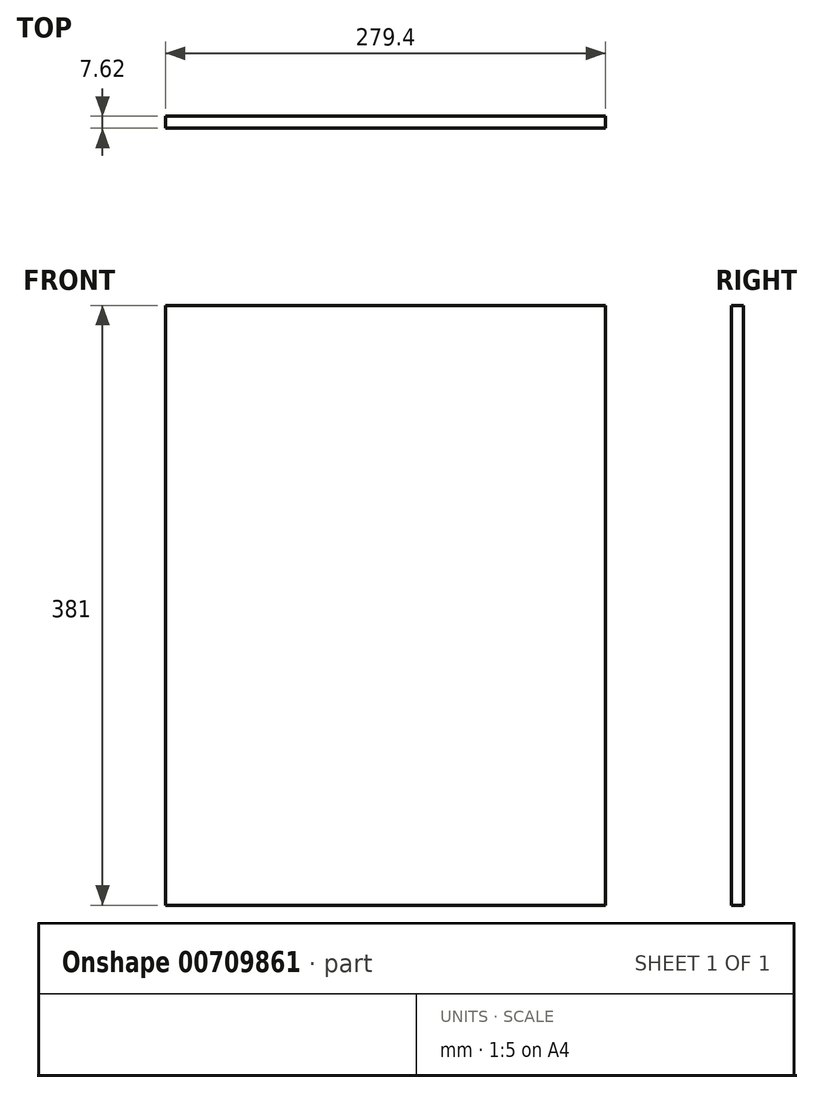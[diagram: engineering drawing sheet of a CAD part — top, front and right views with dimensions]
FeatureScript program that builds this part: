
annotation { "Feature Type Name" : "Feature", "Feature Type Description" : "" }
export const myFeature = defineFeature(function(context is Context, id is Id, definition is map)
    precondition{}
    {
        {
            var Q0;
            Q0=qCreatedBy(makeId("Front.planeOp"),FACE);
            var sketch = newSketch(context, id + "F0", { "sketchPlane" : qUnion([Q0])});
            skLineSegment(sketch, "E0.bottom", {"start": v(-157.96, 45.7) * mm, "end": v(121.44, 45.7) * mm});
            skLineSegment(sketch, "E0.top", {"start": v(-157.96, -335.3) * mm, "end": v(121.44, -335.3) * mm});
            skLineSegment(sketch, "E0.left", {"start": v(-157.96, 45.7) * mm, "end": v(-157.96, -335.3) * mm});
            skLineSegment(sketch, "E0.right", {"start": v(121.44, 45.7) * mm, "end": v(121.44, -335.3) * mm});
            skSolve(sketch);
        }
        {
            var Q0;
            Q0=makeQuery(id+"F0.imprint","IMPRINT",FACE,{"disambiguationData":[TD([[makeQuery(id+"F0.imprint","IMPRINT",EDGE,{"derivedFrom":sQuery(id+"F0.wireOp",EDGE,"E0.bottom")}),-1.0]])]});
            extrude(context, id + "F1", {"entities" : qUnion([Q0]), "depth" : 7.62 * mm, "offsetDistance" : 25.4 * mm});
        }
    });
